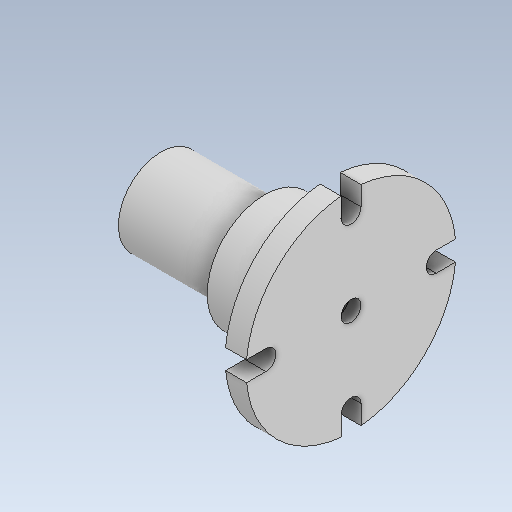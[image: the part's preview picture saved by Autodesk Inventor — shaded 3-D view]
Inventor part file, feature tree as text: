
AUTODESK INVENTOR PART (.ipt)
format: ipt  version: 2021 (Build 250183000, 183)  size: 233,472 bytes
history: native  units: mm
features: extrude x13, sketch x12, projected_geometry x4, plane x1
ambient origin geometry x8: Origin, YZ Plane, XZ Plane, XY Plane, X Axis, Y Axis, Z Axis, Center Point
bodies: Solid1 (feature_tree)
feature tree (30):
  sketch  "Sketch1"  dims[d0=38.5mm d1=34.5mm]
  extrude  "Extrusion1"  Depth=34.5mm
  extrude  "Extrusion2"  Depth=71.0mm TaperAngle=0.0deg
  extrude  "Extrusion3"  Depth=34.0mm TaperAngle=0.0deg
  extrude  "Extrusion4"  Depth=85.0mm
  extrude  "Extrusion5"  Depth=8.1mm
  extrude  "Extrusion6"  Depth=34.5mm
  plane  "Work Plane1"
  extrude  "Extrusion7"  Depth=8.1mm TaperAngle=360.0deg
  extrude  "Extrusion8"  Depth=46.5mm
  extrude  "Extrusion9"  Depth=5.0mm TaperAngle=0.0deg
  extrude  "Extrusion10"  Depth=1.0mm TaperAngle=0.0deg
  extrude  "Extrusion11"  Depth=2.5mm TaperAngle=360.0deg
  extrude  "Extrusion12"  [1 undecoded]
  extrude  "Extrusion13"  [1 undecoded]
  sketch  "Sketch12"  dims[d42=2.5mm d43=0.0mm]
  sketch  "Sketch2"  dims[d2=5.0mm d3=0.0mm d4=71.0mm d5=0.0mm]
  sketch  "Sketch3"  dims[d6=44.5mm d7=34.0mm d8=0.0mm]
  sketch  "Sketch4"  dims[d10=0.0mm d11=0.0mm d12=85.0mm]
  sketch  "Sketch5"  dims[d13=5.0mm d14=0.0mm d15=8.1mm]
  sketch  "Sketch6"  dims[d16=4.0mm d17=0.0mm d19=34.5mm]
  sketch  "Sketch7"  dims[d20=8.1mm d21=40.0mm d23=360.0deg]
  projected_geometry  "Projected Loop1"
  sketch  "Sketch8"  dims[d25=0.0mm d26=0.0mm d27=46.5mm]
  projected_geometry  "Projected Loop2"
  sketch  "Sketch9"  dims[d28=10.0mm d29=0.0mm d30=5.0mm d31=0.0mm]
  projected_geometry  "Projected Loop3"
  sketch  "Sketch10"  dims[d32=5.0mm d33=0.0mm d34=1.0mm d35=0.0mm]
  projected_geometry  "Projected Loop4"
  sketch  "Sketch11"  dims[d36=2.5mm d37=0.0mm d38=40.0mm d40=360.0deg]
note: 2 required parameter values undecoded (feature->parameter linkage not recoverable at this tier; creation-order binding heuristic only, values carry confidence <= 0.55)
